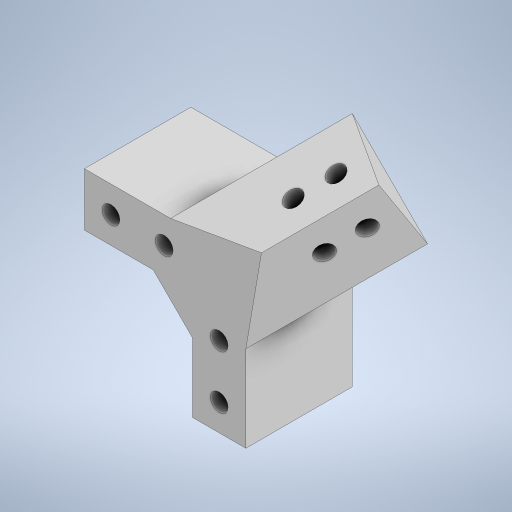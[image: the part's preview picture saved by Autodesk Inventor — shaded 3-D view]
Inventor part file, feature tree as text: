
AUTODESK INVENTOR PART (.ipt)
format: ipt  version: 2024.3 (Build 283343000, 343)  size: 352,768 bytes
history: native  units: mm
features: sketch x10, extrude x7, projected_geometry x6, hole x3, other x1
ambient origin geometry x8: Origin, YZ Plane, XZ Plane, XY Plane, X Axis, Y Axis, Z Axis, Center Point
bodies: Body1 (feature_tree)
feature tree (27):
  other  "ソリッド1"
  extrude  "押し出し1"  Depth=60.0mm
  hole  "穴1"  [1 undecoded]
  extrude  "押し出し2"  Depth=30.0mm TaperAngle=0.0deg
  extrude  "押し出し11"  Depth=7.5mm
  extrude  "押し出し12"  Depth=7.5mm
  extrude  "押し出し13"  Depth=10.5mm
  extrude  "押し出し14"  Depth=10.5mm
  extrude  "押し出し15"  Depth=15.0mm
  hole  "穴2"  [1 undecoded]
  hole  "穴3"  [1 undecoded]
  sketch  "スケッチ1"
  sketch  "スケッチ2"
  sketch  "スケッチ3"
  projected_geometry  "投影ループ1"
  sketch  "スケッチ15"
  projected_geometry  "投影ループ10"
  sketch  "スケッチ16"
  projected_geometry  "投影ループ11"
  sketch  "スケッチ18"
  projected_geometry  "投影ループ13"
  sketch  "スケッチ19"
  projected_geometry  "投影ループ14"
  sketch  "スケッチ20"
  projected_geometry  "投影ループ15"
  sketch  "スケッチ23"
  sketch  "スケッチ24"
note: 3 required parameter values undecoded (feature->parameter linkage not recoverable at this tier; creation-order binding heuristic only, values carry confidence <= 0.55)
